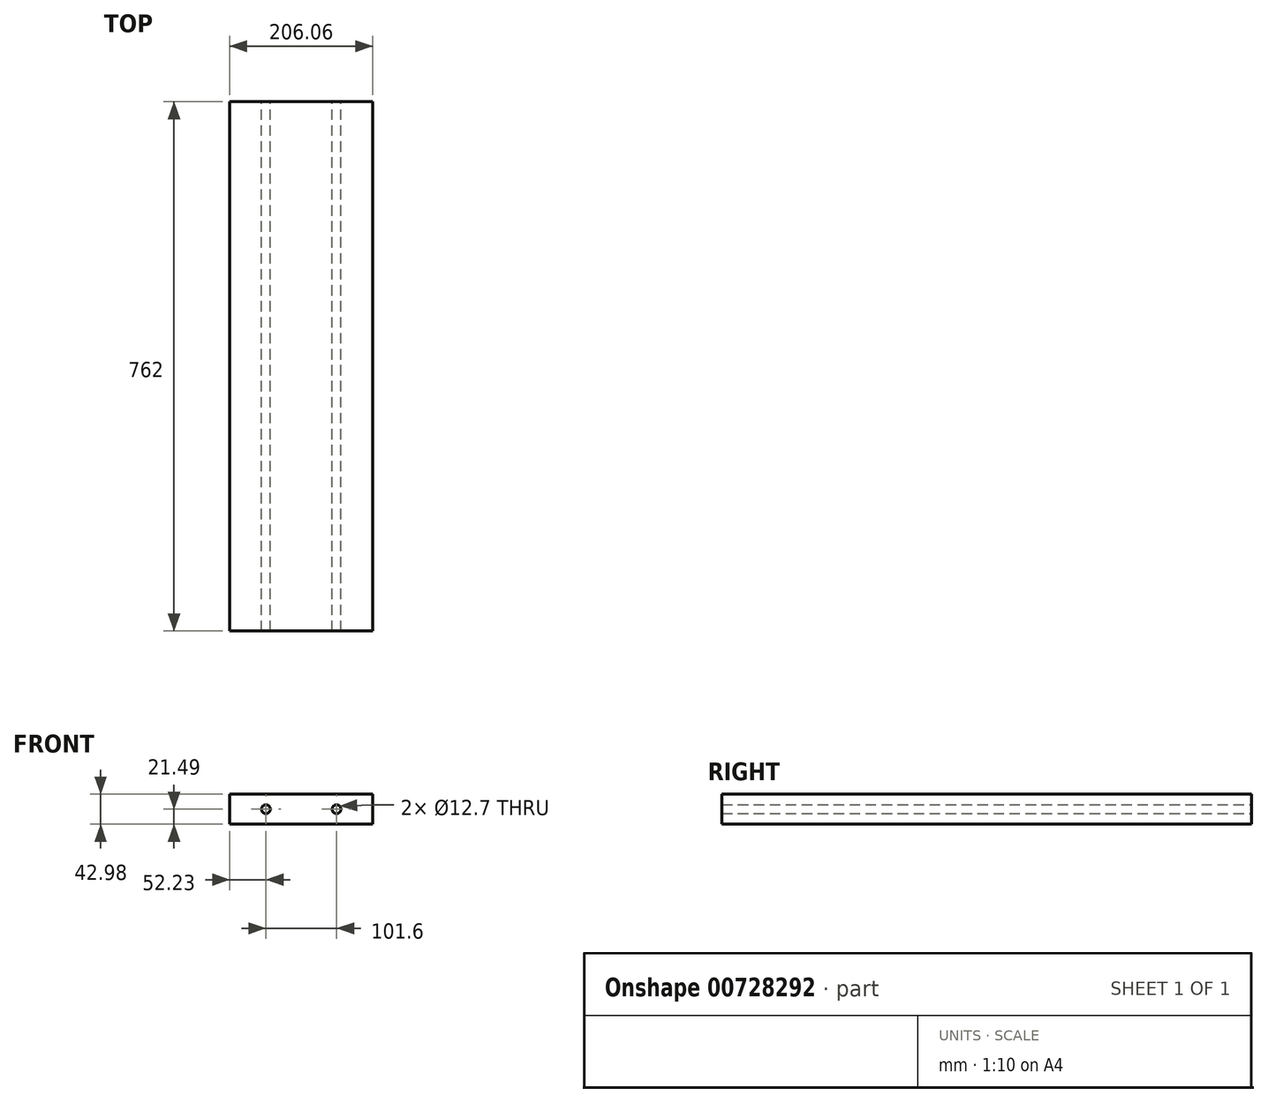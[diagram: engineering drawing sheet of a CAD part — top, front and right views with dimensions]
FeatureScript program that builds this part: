
annotation { "Feature Type Name" : "Feature", "Feature Type Description" : "" }
export const myFeature = defineFeature(function(context is Context, id is Id, definition is map)
    precondition{}
    {
        {
            var Q0;
            Q0=qCreatedBy(makeId("Front.planeOp"),FACE);
            var sketch = newSketch(context, id + "F0", { "sketchPlane" : qUnion([Q0])});
            skLineSegment(sketch, "E0.bottom", {"start": v(-153.83, -21.5) * mm, "end": v(52.23, -21.5) * mm});
            skLineSegment(sketch, "E0.top", {"start": v(-153.83, 21.5) * mm, "end": v(52.23, 21.5) * mm});
            skLineSegment(sketch, "E0.left", {"start": v(-153.83, -21.5) * mm, "end": v(-153.83, 21.5) * mm});
            skPoint(sketch, "E0.middle", {"position": v(0, 0) * mm});
            skLineSegment(sketch, "E1", {"start": v(-101.6, 21.5) * mm, "end": v(-101.6, -21.5) * mm, "construction": true});
            skCircle(sketch, "E2", {"center": v(0, 0) * mm, "radius": 6.35 * mm});
            skCircle(sketch, "E3", {"center": v(-101.6, 0) * mm, "radius": 6.35 * mm});
            skLineSegment(sketch, "E4", {"start": v(52.23, 21.5) * mm, "end": v(52.23, -21.5) * mm});
            skSolve(sketch);
        }
        {
            var Q0;
            Q0=qSketchRegion(id+"F0",true);
            extrude(context, id + "F1", {"entities" : qUnion([Q0]), "depth" : 762 * mm, "offsetDistance" : 25.4 * mm});
        }
    });
